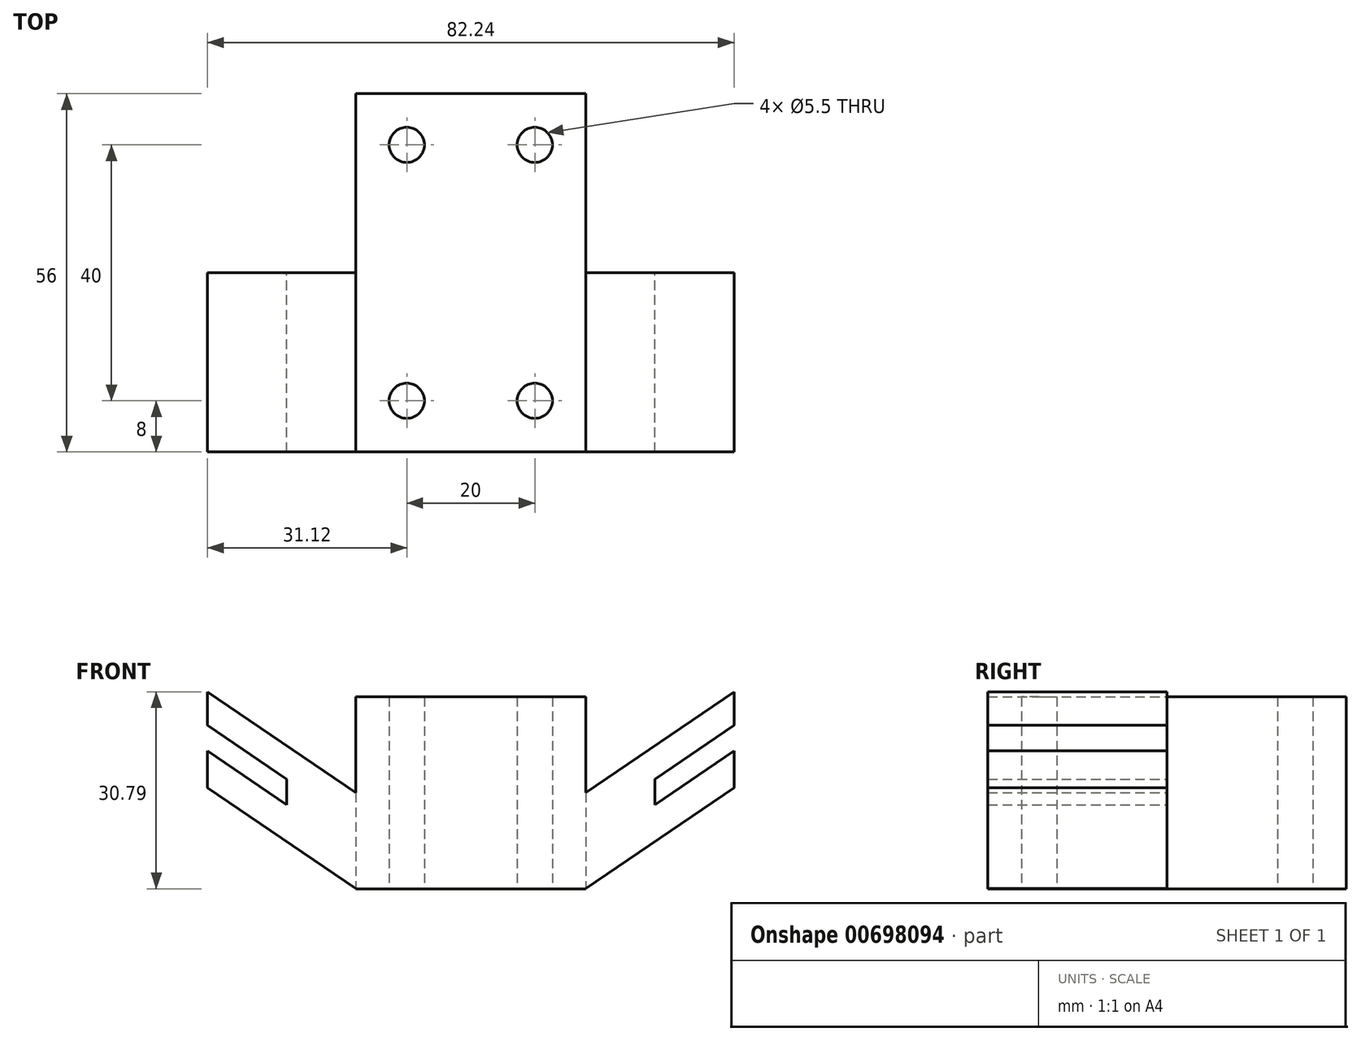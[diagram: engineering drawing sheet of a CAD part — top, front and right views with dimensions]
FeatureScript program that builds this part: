
annotation { "Feature Type Name" : "Feature", "Feature Type Description" : "" }
export const myFeature = defineFeature(function(context is Context, id is Id, definition is map)
    precondition{}
    {
        {
            var Q0;
            Q0=qCreatedBy(makeId("Top.planeOp"),FACE);
            var sketch = newSketch(context, id + "F0", { "sketchPlane" : qUnion([Q0])});
            skLineSegment(sketch, "E0.bottom", {"start": v(-10, 20) * mm, "end": v(10, 20) * mm, "construction": true});
            skLineSegment(sketch, "E0.top", {"start": v(-10, -20) * mm, "end": v(10, -20) * mm, "construction": true});
            skLineSegment(sketch, "E0.left", {"start": v(-10, 20) * mm, "end": v(-10, -20) * mm, "construction": true});
            skLineSegment(sketch, "E0.right", {"start": v(10, 20) * mm, "end": v(10, -20) * mm, "construction": true});
            skPoint(sketch, "E0.middle", {"position": v(0, 0) * mm});
            skLineSegment(sketch, "E1.0", {"start": v(-18, 28) * mm, "end": v(18, 28) * mm});
            skLineSegment(sketch, "E1.1", {"start": v(-18, 28) * mm, "end": v(-18, -28) * mm});
            skLineSegment(sketch, "E1.2", {"start": v(-18, -28) * mm, "end": v(18, -28) * mm});
            skLineSegment(sketch, "E1.3", {"start": v(18, 28) * mm, "end": v(18, -28) * mm});
            skSolve(sketch);
        }
        {
            var Q0;
            Q0=makeQuery(id+"F0.imprint","IMPRINT",FACE,{"disambiguationData":[TD([[makeQuery(id+"F0.imprint","IMPRINT",EDGE,{"derivedFrom":sQuery(id+"F0.wireOp",EDGE,"E1.0")}),-1.0]])]});
            extrude(context, id + "F1", {"entities" : qUnion([Q0]), "depth" : 15 * mm, "offsetDistance" : 25 * mm});
        }
        {
            var Q0;
            Q0=qCreatedBy(makeId("Front.planeOp"),FACE);
            var sketch = newSketch(context, id + "F2", { "sketchPlane" : qUnion([Q0])});
            skLineSegment(sketch, "E2", {"start": v(-18, 15) * mm, "end": v(-41.12, 30.79) * mm});
            skLineSegment(sketch, "E3", {"start": v(-41.12, 30.79) * mm, "end": v(-41.12, 25.56) * mm});
            skLineSegment(sketch, "E4", {"start": v(-41.12, 15.79) * mm, "end": v(-17.94, 0) * mm});
            skLineSegment(sketch, "E5", {"start": v(-41.12, 25.56) * mm, "end": v(-28.74, 17.1) * mm});
            skLineSegment(sketch, "E6", {"start": v(-28.74, 17.1) * mm, "end": v(-28.74, 13.1) * mm});
            skLineSegment(sketch, "E7", {"start": v(-28.74, 13.1) * mm, "end": v(-41.12, 21.56) * mm});
            skLineSegment(sketch, "E8.trimOffspring", {"start": v(-41.12, 21.56) * mm, "end": v(-41.12, 15.79) * mm});
            skLineSegment(sketch, "E9", {"start": v(-18, 15) * mm, "end": v(-17.94, 0) * mm});
            skLineSegment(sketch, "E10.MirrorCS", {"start": v(41.12, 25.56) * mm, "end": v(28.74, 17.1) * mm});
            skLineSegment(sketch, "E11.MirrorCS", {"start": v(28.74, 17.1) * mm, "end": v(28.74, 13.1) * mm});
            skLineSegment(sketch, "E12.MirrorCS", {"start": v(18, 15) * mm, "end": v(41.12, 30.79) * mm});
            skLineSegment(sketch, "E13.MirrorCS", {"start": v(28.74, 13.1) * mm, "end": v(41.12, 21.56) * mm});
            skLineSegment(sketch, "E14.MirrorCS", {"start": v(41.12, 15.79) * mm, "end": v(17.94, 0) * mm});
            skLineSegment(sketch, "E15.MirrorCS", {"start": v(41.12, 21.56) * mm, "end": v(41.12, 15.79) * mm});
            skLineSegment(sketch, "E16.MirrorCS", {"start": v(41.12, 30.79) * mm, "end": v(41.12, 25.56) * mm});
            skLineSegment(sketch, "E17.MirrorCS", {"start": v(18, 15) * mm, "end": v(17.94, 0) * mm});
            skSolve(sketch);
        }
        {
            var Q0;
            Q0=makeQuery(id+"F2.imprint","IMPRINT",FACE,{"disambiguationData":[TD([[makeQuery(id+"F2.imprint","IMPRINT",EDGE,{"derivedFrom":sQuery(id+"F2.wireOp",EDGE,"E2")}),1.0]])]});
            var Q1;
            Q1=makeQuery(id+"F2.imprint","IMPRINT",FACE,{"disambiguationData":[TD([[makeQuery(id+"F2.imprint","IMPRINT",EDGE,{"derivedFrom":sQuery(id+"F2.wireOp",EDGE,"E10.MirrorCS")}),-1.0]])]});
            extrude(context, id + "F3", {"entities" : qUnion([Q0, Q1]), "operationType" : NewBodyOperationType.ADD, "depth" : 28 * mm, "offsetDistance" : 25 * mm});
        }
        {
            var Q0;
            Q0=sQuery(id+"F0.wireOp",VERTEX,"E0.left.end");
            var Q1;
            Q1=sQuery(id+"F0.wireOp",VERTEX,"E0.top.end");
            var Q2;
            Q2=sQuery(id+"F0.wireOp",VERTEX,"E0.right.start");
            var Q3;
            Q3=sQuery(id+"F0.wireOp",VERTEX,"E0.bottom.start");
            var Q4;
            Q4=makeQuery(id+"F1.opExtrude","SWEPT_BODY",BODY,{"disambiguationData":[OSD([sQuery(id+"F0.wireOp",EDGE,"E1.0"),sQuery(id+"F0.wireOp",EDGE,"E1.1"),sQuery(id+"F0.wireOp",EDGE,"E1.2"),sQuery(id+"F0.wireOp",EDGE,"E1.3")])]});
            hole(context, id + "F4", {"style" : HoleStyle.SIMPLE, "endStyle" : HoleEndStyle.THROUGH, "oppositeDirection" : true, "standardTappedOrClearance" : lookupTablePath({ "standard" : "ISO", "fit" : "Normal", "size" : "M5", "type" : "Clearance" }), "standardBlindInLast" : lookupTablePath({ "fit" : "Standard", "standard" : "ISO", "size" : "M5", "type" : "Clearance" }), "holeDiameter" : 5.5 * mm, "majorDiameter" : 5 * mm, "isTappedThrough" : true, "tappedDepth" : 12 * mm, "tapClearance" : 3, "startFromSketch" : true, "locations" : qUnion([Q0, Q1, Q2, Q3]), "scope" : qUnion([Q4])});
        }
        {
            var Q0;
            Q0=makeQuery(id+"F1.opExtrude","CAP_FACE",FACE,{"disambiguationData":[OSD([sQuery(id+"F0.wireOp",EDGE,"E1.0"),sQuery(id+"F0.wireOp",EDGE,"E1.1"),sQuery(id+"F0.wireOp",EDGE,"E1.2"),sQuery(id+"F0.wireOp",EDGE,"E1.3")])],"isStart":false});
            extrude(context, id + "F5", {"entities" : qUnion([Q0]), "operationType" : NewBodyOperationType.ADD, "depth" : 15 * mm, "offsetDistance" : 25 * mm});
        }
    });
